# Revit family: ZEPHYR ROND
name_source: partatom
category: Luminaires
units: mm (PartAtom-declared; Revit-internal decimal feet)

## family parameters
Cote de connecteur circulaire = Utiliser le diamètre
Couper avec des vides une fois chargée = Oui
Hôte = Face
Numéro OmniClass = 23.80.70.11.14.11
Partagée = Oui
Point de calcul de pièce = Oui
Source d'éclairage = Oui
Titre OmniClass = Downlights
Type d'élément = Normal

## types (4) — shared parameters
Angle de l'inclinaison = 60.00°
Emettre la visibilité des formes dans le rendu = Non
Emettre à partir du diamètre du cercle = 610 mm
Fabricant = Résistex
Filtre de couleur = 16777215
Garantie = 5 ans
Gradation des changements de température de couleur de lampe = <Aucun>
IK = 08
IP = 40
Image du type = <Aucun>
Indice de charge = Eclairage
Matériau collerette = PC Transparent
Modèle = Zephyr
Nombre pôles = 1
Tension = 230 V
URL = https://www.resistex-sa.com
Épaisseur = 10 mm  [stored 0.0328084 ft]
Épaisseur collerette = 2 mm  [stored 0.00656168 ft]
zero-valued in all types: Elévation par défaut

## per-type parameters (varying)
| type | Charge apparente | Commentaires relatifs à la puissance | Coût | Description | Diamètre intérieur | Fichier de distribution photométrique | Rayon collerette | Rayon corps |
| 791900 | 15 VA | 13.5W | 42.5 $ | Downlight équipé d'un module LED SMD, efficacité lumineuse de 62.8lm/W | 130 mm  [stored 0.426509 ft] | 791900.ies | 90 mm  [stored 0.295276 ft] | 80 mm |
| 791901 | 15 VA | 13.5W | 42.5 $ | Downlight équipé d'un module LED SMD, efficacité lumineuse de 67lm/W | 130 mm  [stored 0.426509 ft] | 791901.ies | 90 mm  [stored 0.295276 ft] | 80 mm |
| 791902 | 20 VA | 18.8W | 52.5 $ | Downlight équipé d'un module LED SMD, efficacité lumineuse de 75.6lm/W | 173 mm | 791902.ies | 120 mm  [stored 0.393701 ft] | 106 mm |
| 791903 | 20 VA | 18.8W | 52.5 $ | Downlight équipé d'un module LED SMD, efficacité lumineuse de 80.8lm/W | 173 mm | 791903.ies | 120 mm  [stored 0.393701 ft] | 106 mm |

note: [stored X ft] marks values corroborated as IEEE doubles in the binary element streams (Revit-internal decimal feet)
